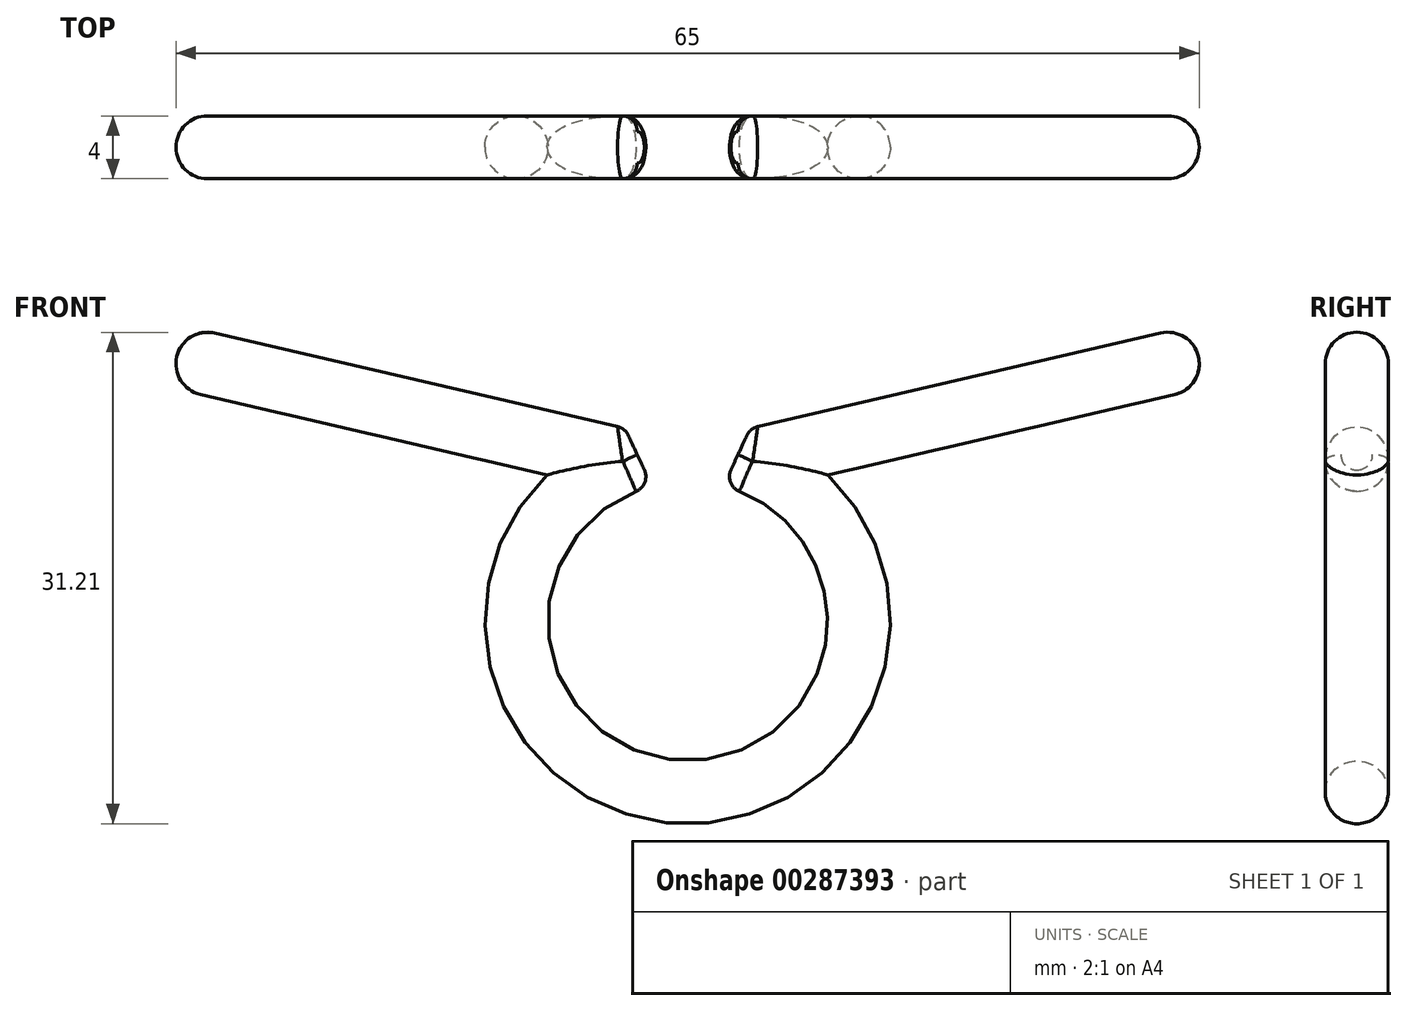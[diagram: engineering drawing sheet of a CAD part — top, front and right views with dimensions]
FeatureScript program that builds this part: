
annotation { "Feature Type Name" : "Feature", "Feature Type Description" : "" }
export const myFeature = defineFeature(function(context is Context, id is Id, definition is map)
    precondition{}
    {
        {
            var Q0;
            Q0=qCreatedBy(makeId("Front.planeOp"),FACE);
            var sketch = newSketch(context, id + "F0", { "sketchPlane" : qUnion([Q0])});
            skArc(sketch, "E0", {"start": v(-2.28, 8.58) * mm, "mid": v(0, -8.88) * mm, "end": v(2.28, 8.58) * mm});
            skArc(sketch, "E1.0", {"start": v(-8.92, 9.28) * mm, "mid": v(0, -12.88) * mm, "end": v(8.92, 9.28) * mm});
            skLineSegment(sketch, "E2", {"start": v(-3.98, 12.24) * mm, "end": v(-32, 18.74) * mm});
            skLineSegment(sketch, "E3", {"start": v(-32, 18.74) * mm, "end": v(-32.9, 14.85) * mm});
            skLineSegment(sketch, "E4", {"start": v(-32.9, 14.85) * mm, "end": v(-8.92, 9.28) * mm});
            skLineSegment(sketch, "E5", {"start": v(-3.98, 12.24) * mm, "end": v(-2.28, 8.58) * mm});
            skLineSegment(sketch, "E6.MirrorCS", {"start": v(3.98, 12.24) * mm, "end": v(2.28, 8.58) * mm});
            skLineSegment(sketch, "E7.MirrorCS", {"start": v(32.9, 14.85) * mm, "end": v(8.92, 9.28) * mm});
            skLineSegment(sketch, "E8.MirrorCS", {"start": v(32, 18.74) * mm, "end": v(32.9, 14.85) * mm});
            skLineSegment(sketch, "E9.MirrorCS", {"start": v(3.98, 12.24) * mm, "end": v(32, 18.74) * mm});
            skSolve(sketch);
        }
        {
            var Q0;
            Q0=makeQuery(id+"F0.imprint","IMPRINT",FACE,{"disambiguationData":[TD([[makeQuery(id+"F0.imprint","IMPRINT",EDGE,{"derivedFrom":sQuery(id+"F0.wireOp",EDGE,"E0")}),-1.0]])]});
            extrude(context, id + "F1", {"entities" : qUnion([Q0]), "depth" : 2 * mm, "hasSecondDirection" : true, "secondDirectionOppositeDirection" : true, "secondDirectionDepth" : 2 * mm});
        }
        {
            var Q0;
            Q0=makeQuery(id+"F1.opExtrude","CAP_EDGE",EDGE,{"disambiguationData":[OSD([sQuery(id+"F0.wireOp",EDGE,"E0")])],"isStart":false});
            var Q1;
            Q1=makeQuery(id+"F1.opExtrude","CAP_EDGE",EDGE,{"disambiguationData":[OSD([sQuery(id+"F0.wireOp",EDGE,"E0")])],"isStart":true});
            var Q2;
            Q2=makeQuery(id+"F1.opExtrude","CAP_EDGE",EDGE,{"disambiguationData":[OSD([sQuery(id+"F0.wireOp",EDGE,"E1.0")])],"isStart":false});
            var Q3;
            Q3=makeQuery(id+"F1.opExtrude","CAP_EDGE",EDGE,{"disambiguationData":[OSD([sQuery(id+"F0.wireOp",EDGE,"E1.0")])],"isStart":true});
            var Q4;
            Q4=makeQuery(id+"F1.opExtrude","CAP_EDGE",EDGE,{"disambiguationData":[OSD([sQuery(id+"F0.wireOp",EDGE,"E4")])],"isStart":false});
            var Q5;
            Q5=makeQuery(id+"F1.opExtrude","CAP_EDGE",EDGE,{"disambiguationData":[OSD([sQuery(id+"F0.wireOp",EDGE,"E2")])],"isStart":false});
            var Q6;
            Q6=makeQuery(id+"F1.opExtrude","CAP_EDGE",EDGE,{"disambiguationData":[OSD([sQuery(id+"F0.wireOp",EDGE,"E2")])],"isStart":true});
            var Q7;
            Q7=makeQuery(id+"F1.opExtrude","CAP_EDGE",EDGE,{"disambiguationData":[OSD([sQuery(id+"F0.wireOp",EDGE,"E4")])],"isStart":true});
            var Q8;
            Q8=makeQuery(id+"F1.opExtrude","CAP_EDGE",EDGE,{"disambiguationData":[OSD([sQuery(id+"F0.wireOp",EDGE,"E3")])],"isStart":true});
            var Q9;
            Q9=makeQuery(id+"F1.opExtrude","CAP_EDGE",EDGE,{"disambiguationData":[OSD([sQuery(id+"F0.wireOp",EDGE,"E3")])],"isStart":false});
            var Q10;
            Q10=makeQuery(id+"F1.opExtrude","SWEPT_EDGE",EDGE,{"disambiguationData":[OSD([sQuery(id+"F0.wireOp",EDGE,"E3"),sQuery(id+"F0.wireOp",EDGE,"E4")])]});
            var Q11;
            Q11=makeQuery(id+"F1.opExtrude","SWEPT_EDGE",EDGE,{"disambiguationData":[OSD([sQuery(id+"F0.wireOp",EDGE,"E2"),sQuery(id+"F0.wireOp",EDGE,"E3")])]});
            var Q12;
            Q12=makeQuery(id+"F1.opExtrude","CAP_EDGE",EDGE,{"disambiguationData":[OSD([sQuery(id+"F0.wireOp",EDGE,"E9.MirrorCS")])],"isStart":false});
            var Q13;
            Q13=makeQuery(id+"F1.opExtrude","CAP_EDGE",EDGE,{"disambiguationData":[OSD([sQuery(id+"F0.wireOp",EDGE,"E9.MirrorCS")])],"isStart":true});
            var Q14;
            Q14=makeQuery(id+"F1.opExtrude","CAP_EDGE",EDGE,{"disambiguationData":[OSD([sQuery(id+"F0.wireOp",EDGE,"E7.MirrorCS")])],"isStart":false});
            var Q15;
            Q15=makeQuery(id+"F1.opExtrude","CAP_EDGE",EDGE,{"disambiguationData":[OSD([sQuery(id+"F0.wireOp",EDGE,"E8.MirrorCS")])],"isStart":false});
            var Q16;
            Q16=makeQuery(id+"F1.opExtrude","SWEPT_EDGE",EDGE,{"disambiguationData":[OSD([sQuery(id+"F0.wireOp",EDGE,"E8.MirrorCS"),sQuery(id+"F0.wireOp",EDGE,"E9.MirrorCS")])]});
            var Q17;
            Q17=makeQuery(id+"F1.opExtrude","CAP_EDGE",EDGE,{"disambiguationData":[OSD([sQuery(id+"F0.wireOp",EDGE,"E8.MirrorCS")])],"isStart":true});
            var Q18;
            Q18=makeQuery(id+"F1.opExtrude","SWEPT_EDGE",EDGE,{"disambiguationData":[OSD([sQuery(id+"F0.wireOp",EDGE,"E7.MirrorCS"),sQuery(id+"F0.wireOp",EDGE,"E8.MirrorCS")])]});
            var Q19;
            Q19=makeQuery(id+"F1.opExtrude","CAP_EDGE",EDGE,{"disambiguationData":[OSD([sQuery(id+"F0.wireOp",EDGE,"E7.MirrorCS")])],"isStart":true});
            fillet(context, id + "F2", {"entities" : qUnion([Q0, Q1, Q2, Q3, Q4, Q5, Q6, Q7, Q8, Q9, Q10, Q11, Q12, Q13, Q14, Q15, Q16, Q17, Q18, Q19]), "radius" : 2 * mm, "tangentPropagation" : true, "allowEdgeOverflow" : false});
        }
        {
            var Q0;
            Q0=makeQuery(id+"F1.opExtrude","SWEPT_FACE",FACE,{"disambiguationData":[OSD([sQuery(id+"F0.wireOp",EDGE,"E6.MirrorCS")])]});
            var Q1;
            Q1=makeQuery(id+"F1.opExtrude","SWEPT_FACE",FACE,{"disambiguationData":[OSD([sQuery(id+"F0.wireOp",EDGE,"E5")])]});
            fillet(context, id + "F3", {"entities" : qUnion([Q0, Q1]), "radius" : 1 * mm, "tangentPropagation" : true, "allowEdgeOverflow" : false});
        }
    });
